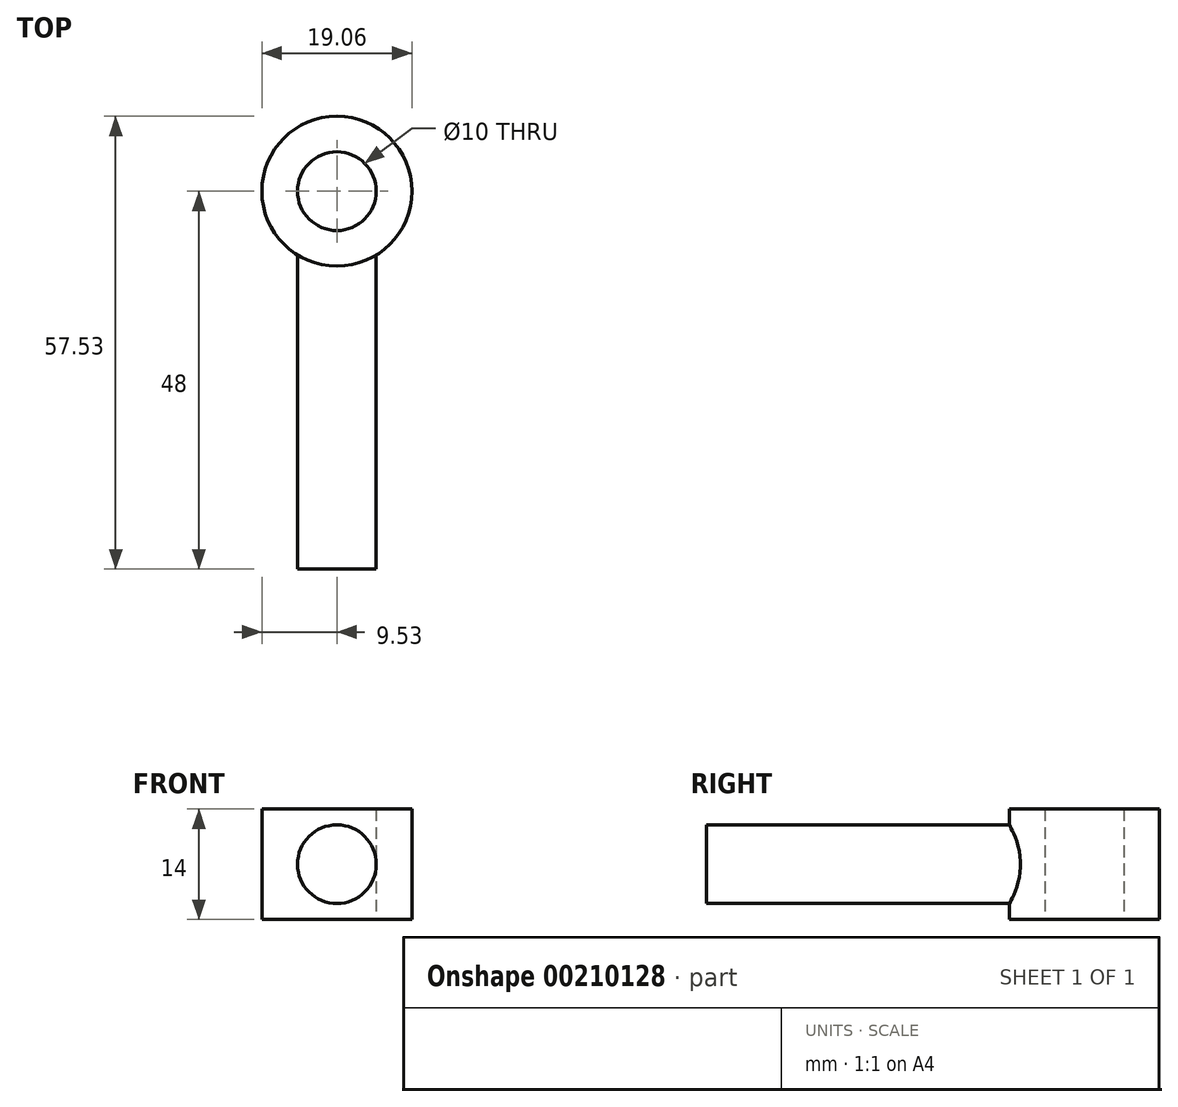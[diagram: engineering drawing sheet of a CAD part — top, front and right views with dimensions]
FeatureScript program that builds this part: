
annotation { "Feature Type Name" : "Feature", "Feature Type Description" : "" }
export const myFeature = defineFeature(function(context is Context, id is Id, definition is map)
    precondition{}
    {
        {
            var Q0;
            Q0=qCreatedBy(makeId("Top.planeOp"),FACE);
            var sketch = newSketch(context, id + "F0", { "sketchPlane" : qUnion([Q0])});
            skCircle(sketch, "E0", {"center": v(0, 0) * mm, "radius": 5 * mm});
            skCircle(sketch, "E1", {"center": v(0, 0) * mm, "radius": 9.53 * mm});
            skSolve(sketch);
        }
        {
            var Q0;
            Q0 = qSketchRegion(id + "F0", true);
            extrude(context, id + "F1", {"entities" : qUnion([Q0]), "endBound" : BoundingType.SYMMETRIC, "depth" : 14 * mm});
        }
        {
            var Q0;
            Q0=qCreatedBy(makeId("Front.planeOp"),FACE);
            var sketch = newSketch(context, id + "F2", { "sketchPlane" : qUnion([Q0])});
            skCircle(sketch, "E2", {"center": v(0, 0) * mm, "radius": 5 * mm});
            skSolve(sketch);
        }
        {
            var Q0;
            Q0 = qSketchRegion(id + "F2", true);
            extrude(context, id + "F3", {"entities" : qUnion([Q0]), "operationType" : NewBodyOperationType.ADD, "depth" : 48 * mm});
        }
        {
            var Q0;
            Q0=qCreatedBy(makeId("Top.planeOp"),FACE);
            var sketch = newSketch(context, id + "F4", { "sketchPlane" : qUnion([Q0])});
            skCircle(sketch, "E3", {"center": v(0, 0) * mm, "radius": 5 * mm});
            skSolve(sketch);
        }
        {
            var Q0;
            Q0 = qSketchRegion(id + "F4", true);
            extrude(context, id + "F5", {"entities" : qUnion([Q0]), "operationType" : NewBodyOperationType.REMOVE, "endBound" : BoundingType.SYMMETRIC, "depth" : 25 * mm});
        }
    });
